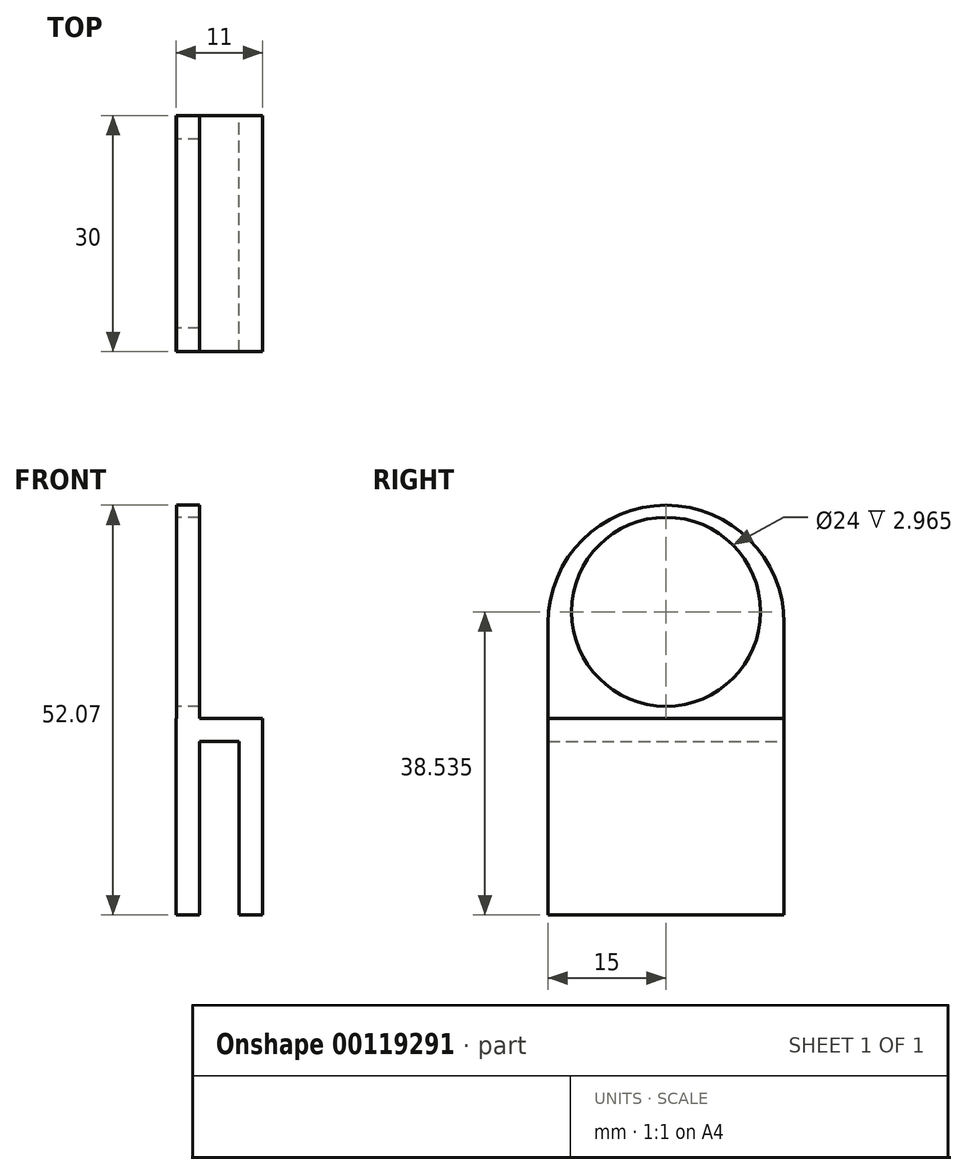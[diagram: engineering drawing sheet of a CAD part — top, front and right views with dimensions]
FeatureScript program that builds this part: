
annotation { "Feature Type Name" : "Feature", "Feature Type Description" : "" }
export const myFeature = defineFeature(function(context is Context, id is Id, definition is map)
    precondition{}
    {
        {
            var Q0;
            Q0=qCreatedBy(makeId("Front.planeOp"),FACE);
            var sketch = newSketch(context, id + "F0", { "sketchPlane" : qUnion([Q0])});
            skLineSegment(sketch, "E0.bottom", {"start": v(-18.93, 27.8) * mm, "end": v(-18.9, 27.8) * mm});
            skLineSegment(sketch, "E0.top", {"start": v(-18.93, 2.8) * mm, "end": v(-15.93, 2.8) * mm});
            skLineSegment(sketch, "E0.left", {"start": v(-18.93, 27.8) * mm, "end": v(-18.93, 2.8) * mm});
            skLineSegment(sketch, "E0.right", {"start": v(-15.93, 24.88) * mm, "end": v(-15.93, 2.8) * mm});
            skLineSegment(sketch, "E1.bottom", {"start": v(-15.93, 27.8) * mm, "end": v(-10.93, 27.8) * mm});
            skLineSegment(sketch, "E1.top", {"start": v(-15.93, 24.88) * mm, "end": v(-10.93, 24.88) * mm});
            skLineSegment(sketch, "E2.bottom", {"start": v(-10.93, 27.8) * mm, "end": v(-7.93, 27.8) * mm});
            skLineSegment(sketch, "E2.top", {"start": v(-10.93, 2.8) * mm, "end": v(-7.93, 2.8) * mm});
            skLineSegment(sketch, "E2.left", {"start": v(-10.93, 24.88) * mm, "end": v(-10.93, 2.8) * mm});
            skLineSegment(sketch, "E2.right", {"start": v(-7.93, 27.8) * mm, "end": v(-7.93, 2.8) * mm});
            skLineSegment(sketch, "E3.top", {"start": v(-18.9, 54.88) * mm, "end": v(-15.93, 54.88) * mm});
            skLineSegment(sketch, "E3.left", {"start": v(-15.93, 27.8) * mm, "end": v(-15.93, 54.88) * mm});
            skLineSegment(sketch, "E3.right", {"start": v(-18.9, 27.8) * mm, "end": v(-18.9, 54.88) * mm});
            skSolve(sketch);
        }
        {
            var Q0;
            Q0=makeQuery(id+"F0.imprint","IMPRINT",FACE,{"disambiguationData":[TD([[makeQuery(id+"F0.imprint","IMPRINT",EDGE,{"derivedFrom":sQuery(id+"F0.wireOp",EDGE,"E0.bottom")}),-1.0]])]});
            extrude(context, id + "F1", {"entities" : qUnion([Q0]), "depth" : 30 * mm});
        }
        {
            var Q0;
            Q0=makeQuery(id+"F1.opExtrude","SWEPT_FACE",FACE,{"disambiguationData":[OSD([sQuery(id+"F0.wireOp",EDGE,"E3.right")])]});
            var sketch = newSketch(context, id + "F2", { "sketchPlane" : qUnion([Q0])});
            skCircle(sketch, "E4", {"center": v(15, 41.34) * mm, "radius": 12 * mm});
            skSolve(sketch);
        }
        {
            var Q0;
            Q0=makeQuery(id+"F2.imprint","IMPRINT",FACE,{"disambiguationData":[TD([[makeQuery(id+"F2.imprint","IMPRINT",EDGE,{"derivedFrom":sQuery(id+"F2.wireOp",EDGE,"E4")}),1.0]])]});
            extrude(context, id + "F3", {"entities" : qUnion([Q0]), "operationType" : NewBodyOperationType.REMOVE, "oppositeDirection" : true, "depth" : 25 * mm});
        }
        {
            var Q0;
            Q0=makeQuery(id+"F1.opExtrude","CAP_EDGE",EDGE,{"disambiguationData":[OSD([sQuery(id+"F0.wireOp",EDGE,"E3.top")])],"isStart":true});
            var Q1;
            Q1=makeQuery(id+"F1.opExtrude","CAP_EDGE",EDGE,{"disambiguationData":[OSD([sQuery(id+"F0.wireOp",EDGE,"E3.top")])],"isStart":false});
            fillet(context, id + "F4", {"entities" : qUnion([Q0, Q1]), "radius" : 15 * mm, "tangentPropagation" : true, "allowEdgeOverflow" : false});
        }
        {
            var Q0;
            Q0=makeQuery(id+"F2.imprint","IMPRINT",FACE,{"disambiguationData":[TD([[makeQuery(id+"F2.imprint","IMPRINT",EDGE,{"derivedFrom":sQuery(id+"F2.wireOp",EDGE,"E4")}),1.0]])]});
            extrude(context, id + "F5", {"entities" : qUnion([Q0]), "operationType" : NewBodyOperationType.REMOVE, "oppositeDirection" : true, "depth" : 7.33 * mm});
        }
    });
